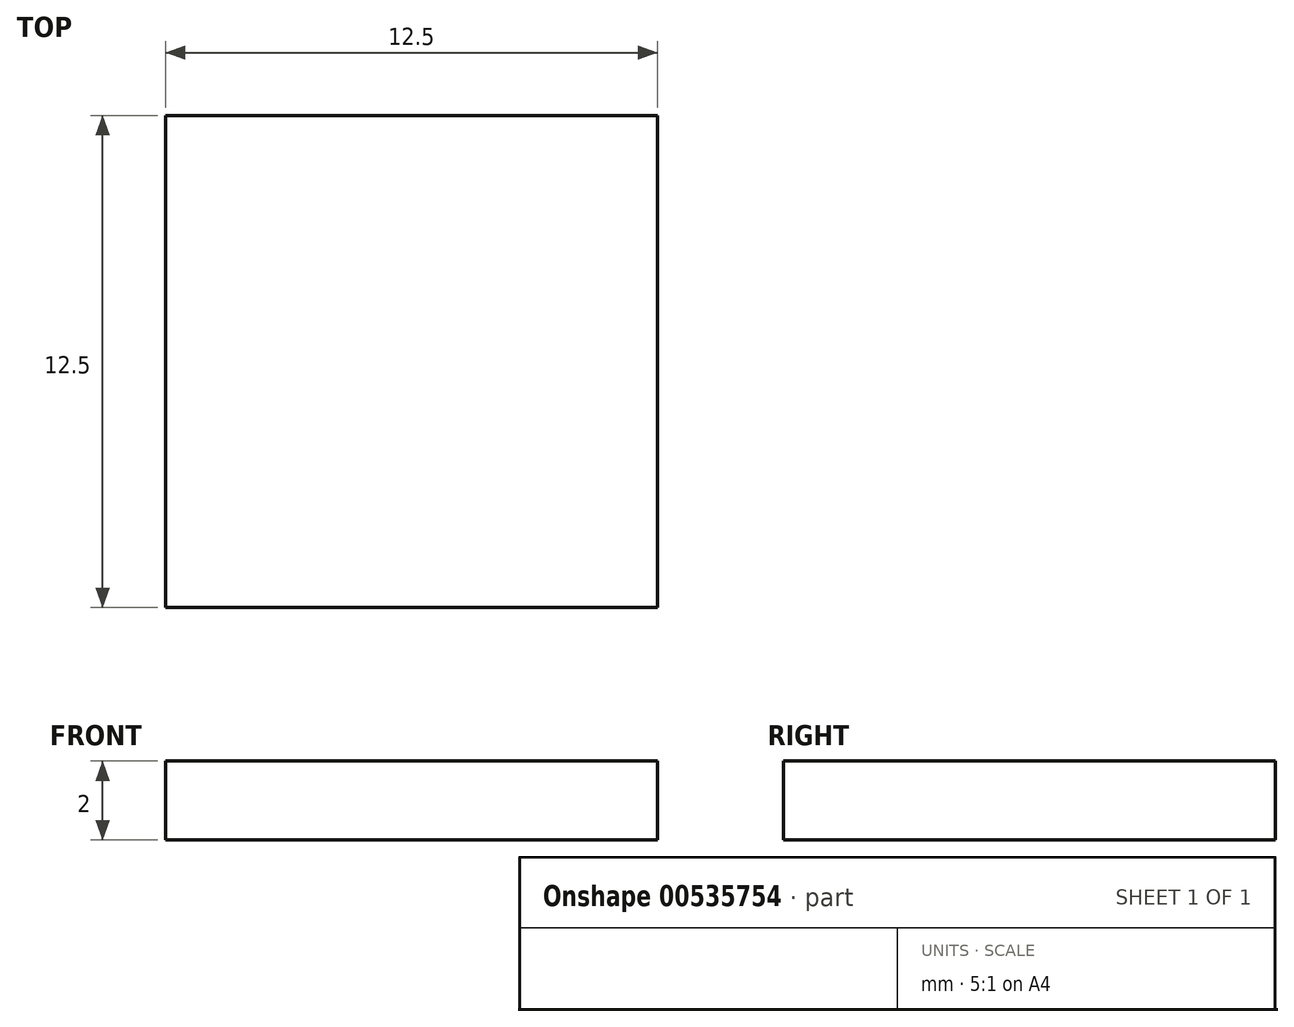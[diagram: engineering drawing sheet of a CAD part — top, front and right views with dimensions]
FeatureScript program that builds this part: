
annotation { "Feature Type Name" : "Feature", "Feature Type Description" : "" }
export const myFeature = defineFeature(function(context is Context, id is Id, definition is map)
    precondition{}
    {
        {
            var Q0;
            Q0=qCreatedBy(makeId("Top.planeOp"),FACE);
            var sketch = newSketch(context, id + "F0", { "sketchPlane" : qUnion([Q0])});
            skLineSegment(sketch, "E0.bottom", {"start": v(6.25, -6.25) * mm, "end": v(-6.25, -6.25) * mm});
            skLineSegment(sketch, "E0.top", {"start": v(6.25, 6.25) * mm, "end": v(-6.25, 6.25) * mm});
            skLineSegment(sketch, "E0.left", {"start": v(6.25, -6.25) * mm, "end": v(6.25, 6.25) * mm});
            skLineSegment(sketch, "E0.right", {"start": v(-6.25, -6.25) * mm, "end": v(-6.25, 6.25) * mm});
            skPoint(sketch, "E0.middle", {"position": v(0, 0) * mm});
            skSolve(sketch);
        }
        {
            var Q0;
            Q0 = qSketchRegion(id + "F0", true);
            extrude(context, id + "F1", {"entities" : qUnion([Q0]), "depth" : 2 * mm, "offsetDistance" : 25 * mm});
        }
    });
